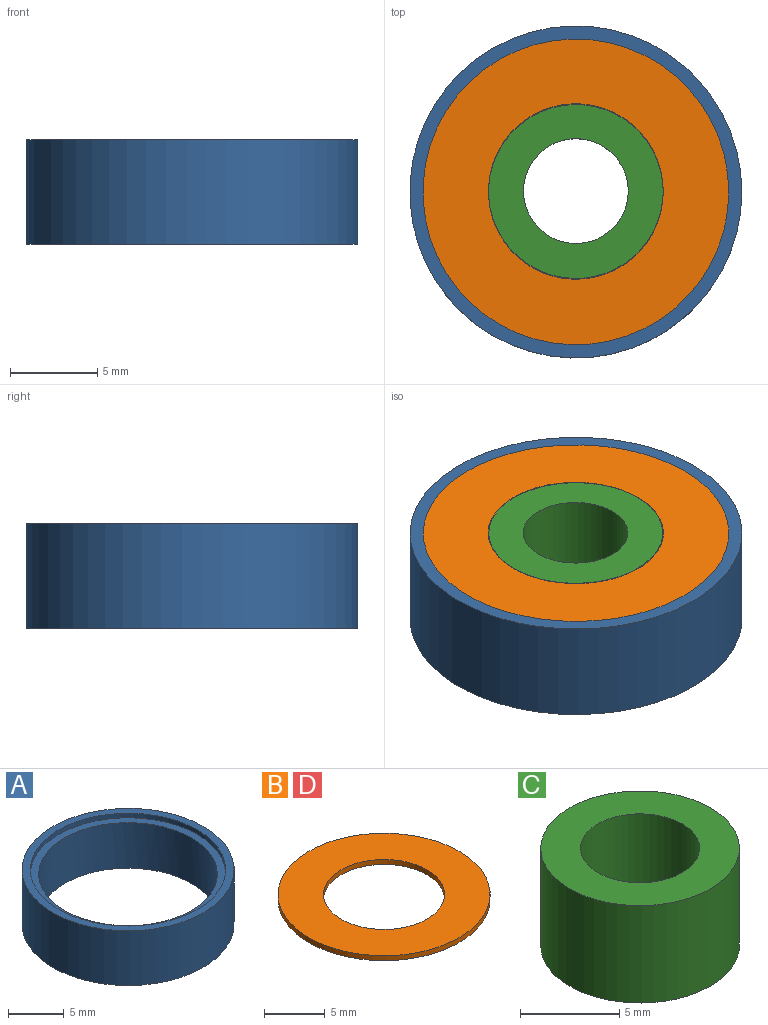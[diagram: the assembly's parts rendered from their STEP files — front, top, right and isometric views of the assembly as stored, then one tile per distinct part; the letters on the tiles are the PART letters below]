
ASSEMBLY  parts=4 mates=3
PART A: 8 faces, bbox 19x19x6 mm
  f0: cylinder r=8mm len=16mm, axis (0,0,-1), area 251.3mm2, adj f5,f7
  f1: cylinder r=9.5mm len=19mm, axis (0,0,-1), area 358.1mm2, adj f2,f3
  f2: plane 19x19mm, normal (0,0,1), area 43mm2, adj f1,f4
  f3: plane 19x19mm, normal (0,0,-1), area 43mm2, adj f1,f6
  f4: cylinder r=8.75mm len=17.5mm, axis (0,0,1), area 27.5mm2, adj f2,f5
  f5: plane 17.5x17.5mm, normal (0,0,1), area 39.5mm2, adj f0,f4
  f6: cylinder r=8.75mm len=17.5mm, axis (0,0,-1), area 27.5mm2, adj f3,f7
  f7: plane 17.5x17.5mm, normal (0,0,-1), area 39.5mm2, adj f0,f6
PART B: 4 faces, bbox 17.5x17.5x0.5 mm
  f0: cylinder r=5mm len=10mm, axis (0,0,-1), area 15.7mm2, adj f2,f3
  f1: cylinder r=8.75mm len=17.5mm, axis (0,0,-1), area 27.5mm2, adj f2,f3
  f2: plane 17.5x17.5mm, normal (0,0,1), area 162mm2, adj f0,f1
  f3: plane 17.5x17.5mm, normal (0,0,-1), area 162mm2, adj f0,f1
PART C: 4 faces, bbox 10x10x6 mm
  f0: cylinder r=3mm len=6mm, axis (0,0,-1), area 113.1mm2, adj f2,f3
  f1: cylinder r=5mm len=10mm, axis (0,0,-1), area 188.5mm2, adj f2,f3
  f2: plane 10x10mm, normal (0,0,1), area 50.3mm2, adj f0,f1
  f3: plane 10x10mm, normal (0,0,-1), area 50.3mm2, adj f0,f1
PART D: same geometry as B
PLACE A at identity
PLACE B t=(0,0,5.5)mm
PLACE C t=(0,0.05,0)mm
PLACE D t=(0,0.05,0)mm
MATE fastened B.f1 <-> A.f4  axis (0,0,-1) through (0,0,5.5)mm
MATE fastened D.f1 <-> A.f6  axis (0,0,1) through (0,0.05,0.5)mm
MATE revolute C.f1 <-> A.f6  axis (0,0,-1) through (0,0.05,0)mm
